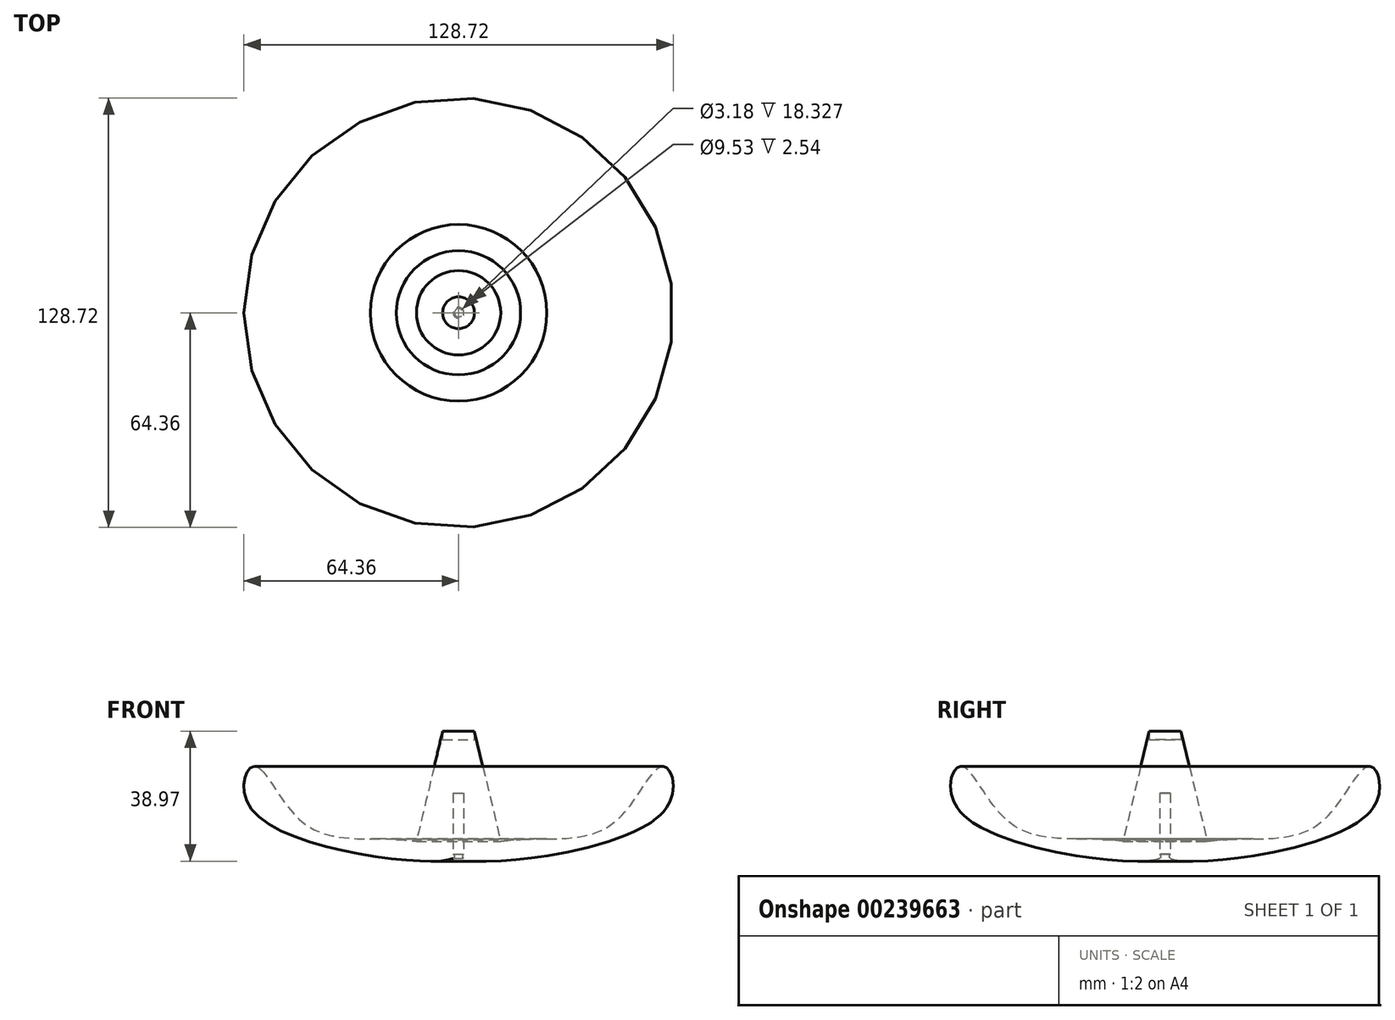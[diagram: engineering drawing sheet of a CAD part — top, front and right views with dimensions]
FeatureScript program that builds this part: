
annotation { "Feature Type Name" : "Feature", "Feature Type Description" : "" }
export const myFeature = defineFeature(function(context is Context, id is Id, definition is map)
    precondition{}
    {
        {
            var Q0;
            Q0=qCreatedBy(makeId("Front.planeOp"),FACE);
            var sketch = newSketch(context, id + "F0", { "sketchPlane" : qUnion([Q0])});
            skLineSegment(sketch, "E0.left", {"start": v(0, 19.56) * mm, "end": v(0, 38.1) * mm});
            skLineSegment(sketch, "E1.bottom", {"start": v(0, 0) * mm, "end": v(1.59, 0) * mm});
            skLineSegment(sketch, "E1.top", {"start": v(0, 19.56) * mm, "end": v(1.59, 19.56) * mm});
            skLineSegment(sketch, "E1.right", {"start": v(1.59, 0) * mm, "end": v(1.59, 19.56) * mm});
            skLineSegment(sketch, "E2.top", {"start": v(0, 35.56) * mm, "end": v(4.76, 35.56) * mm});
            skLineSegment(sketch, "E2.right", {"start": v(4.76, 38.1) * mm, "end": v(4.76, 35.56) * mm});
            skLineSegment(sketch, "E3", {"start": v(61.33, 27.53) * mm, "end": v(59.3, 26.59) * mm});
            skFitSpline(sketch, "E4", {"points": [v(1.59, 0) * mm, v(61.33, 13.83) * mm, v(61.33, 27.53) * mm, v(46.18, 10.33) * mm, v(12.64, 5.1) * mm, v(1.59, 0) * mm]});
            skLineSegment(sketch, "E5", {"start": v(4.76, 38.1) * mm, "end": v(12.64, 5.1) * mm});
            skPoint(sketch, "E6.orphan", {"position": v(12.64, 2.56) * mm});
            skArc(sketch, "E7", {"start": v(26.45, 5.76) * mm, "mid": v(19.53, 5.67) * mm, "end": v(12.64, 5.1) * mm});
            skSolve(sketch);
        }
        {
            var Q0;
            Q0 = qSketchRegion(id + "F0", true);
            var Q1;
            Q1=sQuery(id+"F0.wireOp",EDGE,"E0.left");
            revolve(context, id + "F1", {"entities" : qUnion([Q0]), "axis" : qUnion([Q1]), "revolveType" : RevolveType.FULL});
        }
    });
